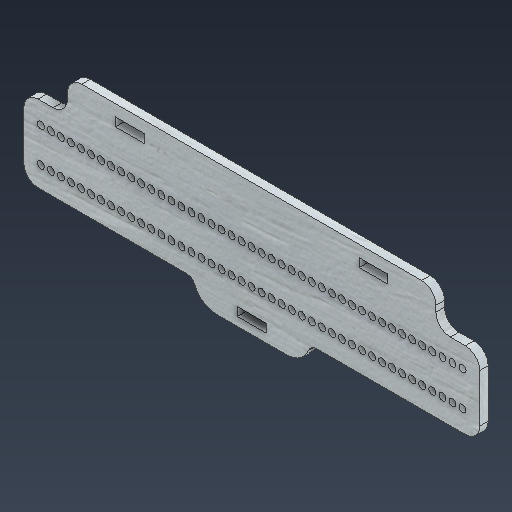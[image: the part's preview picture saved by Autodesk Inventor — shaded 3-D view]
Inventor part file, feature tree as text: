
AUTODESK INVENTOR PART (.ipt)
format: ipt  version: 2025.3 (Build 293356000, 356)  size: 410,624 bytes
history: native  units: mm
features: sketch x3, other x2, extrude x1
ambient origin geometry x8: Origin, YZ Plane, XZ Plane, XY Plane, X Axis, Y Axis, Z Axis, Center Point
bodies: Body1 (feature_tree)
feature tree (6):
  other  "實體1"
  extrude  "擠出1"  Depth=10.0mm
  sketch  "草圖3"
  sketch  "草圖5"
  sketch  "草圖1"
  other  "草圖 - 矩形陣列5"
